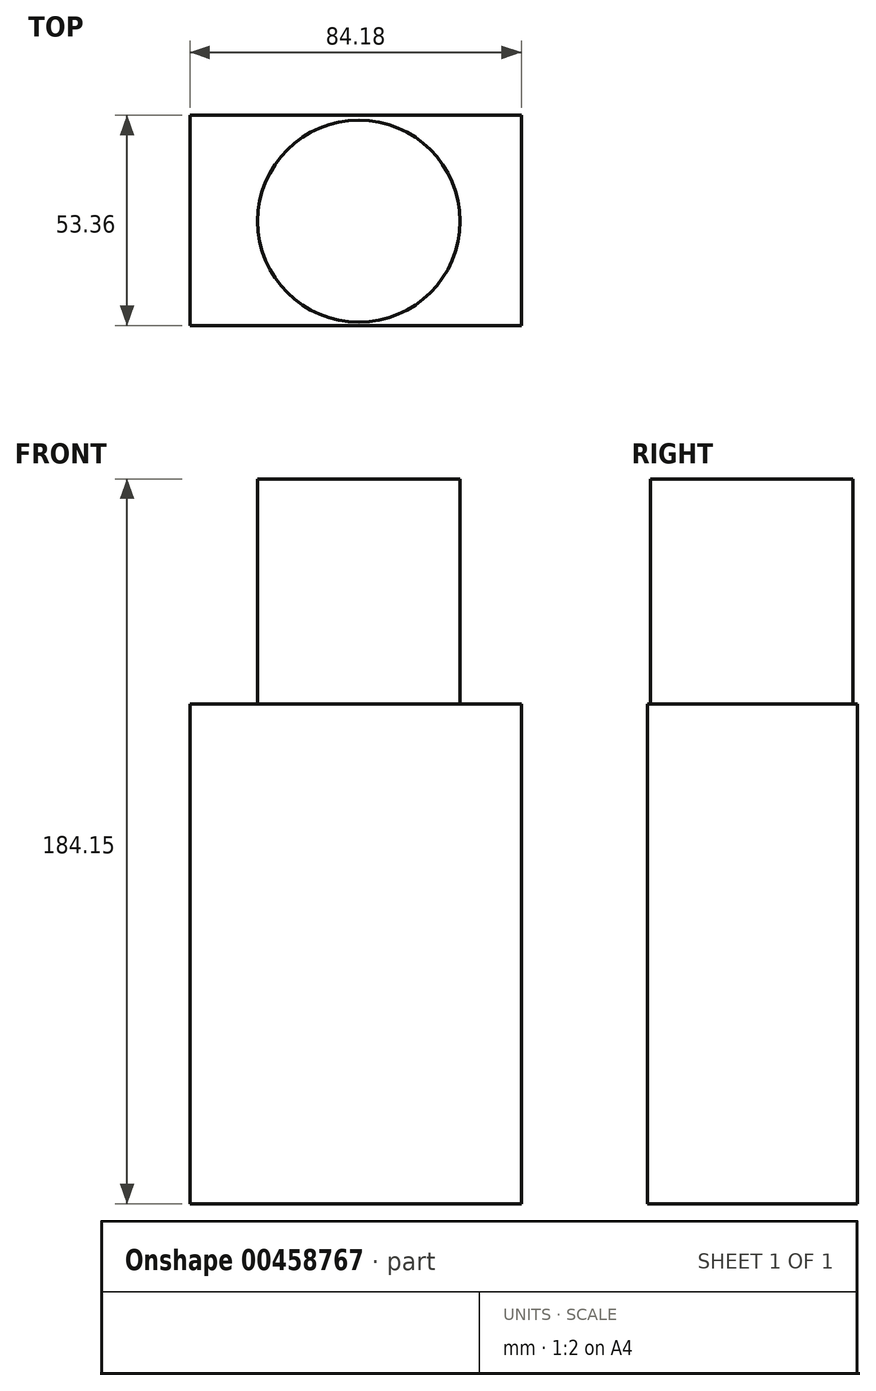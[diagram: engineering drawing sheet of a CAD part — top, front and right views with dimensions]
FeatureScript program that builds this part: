
annotation { "Feature Type Name" : "Feature", "Feature Type Description" : "" }
export const myFeature = defineFeature(function(context is Context, id is Id, definition is map)
    precondition{}
    {
        {
            var Q0;
            Q0=qCreatedBy(makeId("Top.planeOp"),FACE);
            var sketch = newSketch(context, id + "F0", { "sketchPlane" : qUnion([Q0])});
            skCircle(sketch, "E0", {"center": v(0, 0) * mm, "radius": 29.87 * mm});
            skSolve(sketch);
        }
        {
            var Q0;
            Q0 = qSketchRegion(id + "F0", true);
            extrude(context, id + "F1", {"entities" : qUnion([Q0]), "depth" : 101.6 * mm});
        }
        {
            var Q0;
            Q0=makeQuery(id+"F1.opExtrude","SWEPT_BODY",BODY,{"disambiguationData":[OSD([sQuery(id+"F0.wireOp",EDGE,"E0")])]});
            deleteBodies(context, id + "F2", {"entities" : qUnion([Q0])});
        }
        {
            var Q0;
            Q0=qCreatedBy(makeId("Top.planeOp"),FACE);
            var sketch = newSketch(context, id + "F3", { "sketchPlane" : qUnion([Q0])});
            skLineSegment(sketch, "E1.bottom", {"start": v(-42.89, 26.89) * mm, "end": v(41.29, 26.89) * mm});
            skLineSegment(sketch, "E1.top", {"start": v(-42.89, -26.47) * mm, "end": v(41.29, -26.47) * mm});
            skLineSegment(sketch, "E1.left", {"start": v(-42.89, 26.89) * mm, "end": v(-42.89, -26.47) * mm});
            skLineSegment(sketch, "E1.right", {"start": v(41.29, 26.89) * mm, "end": v(41.29, -26.47) * mm});
            skSolve(sketch);
        }
        {
            var Q0;
            Q0=makeQuery(id+"F3.imprint","IMPRINT",FACE,{"disambiguationData":[TD([[makeQuery(id+"F3.imprint","IMPRINT",EDGE,{"derivedFrom":sQuery(id+"F3.wireOp",EDGE,"E1.bottom")}),-1.0]])]});
            extrude(context, id + "F4", {"entities" : qUnion([Q0]), "depth" : 127 * mm});
        }
        {
            var Q0;
            Q0=makeQuery(id+"F4.opExtrude","CAP_FACE",FACE,{"disambiguationData":[OSD([sQuery(id+"F3.wireOp",EDGE,"E1.bottom"),sQuery(id+"F3.wireOp",EDGE,"E1.top"),sQuery(id+"F3.wireOp",EDGE,"E1.left"),sQuery(id+"F3.wireOp",EDGE,"E1.right")])],"isStart":false});
            var sketch = newSketch(context, id + "F5", { "sketchPlane" : qUnion([Q0])});
            skCircle(sketch, "E2", {"center": v(0, 0) * mm, "radius": 25.7 * mm});
            skSolve(sketch);
        }
        {
            var Q0;
            Q0=makeQuery(id+"F5.imprint","IMPRINT",FACE,{"disambiguationData":[TD([[makeQuery(id+"F5.imprint","IMPRINT",EDGE,{"derivedFrom":sQuery(id+"F5.wireOp",EDGE,"E2")}),1.0]])]});
            extrude(context, id + "F6", {"entities" : qUnion([Q0]), "operationType" : NewBodyOperationType.ADD, "depth" : 57.15 * mm});
        }
    });
